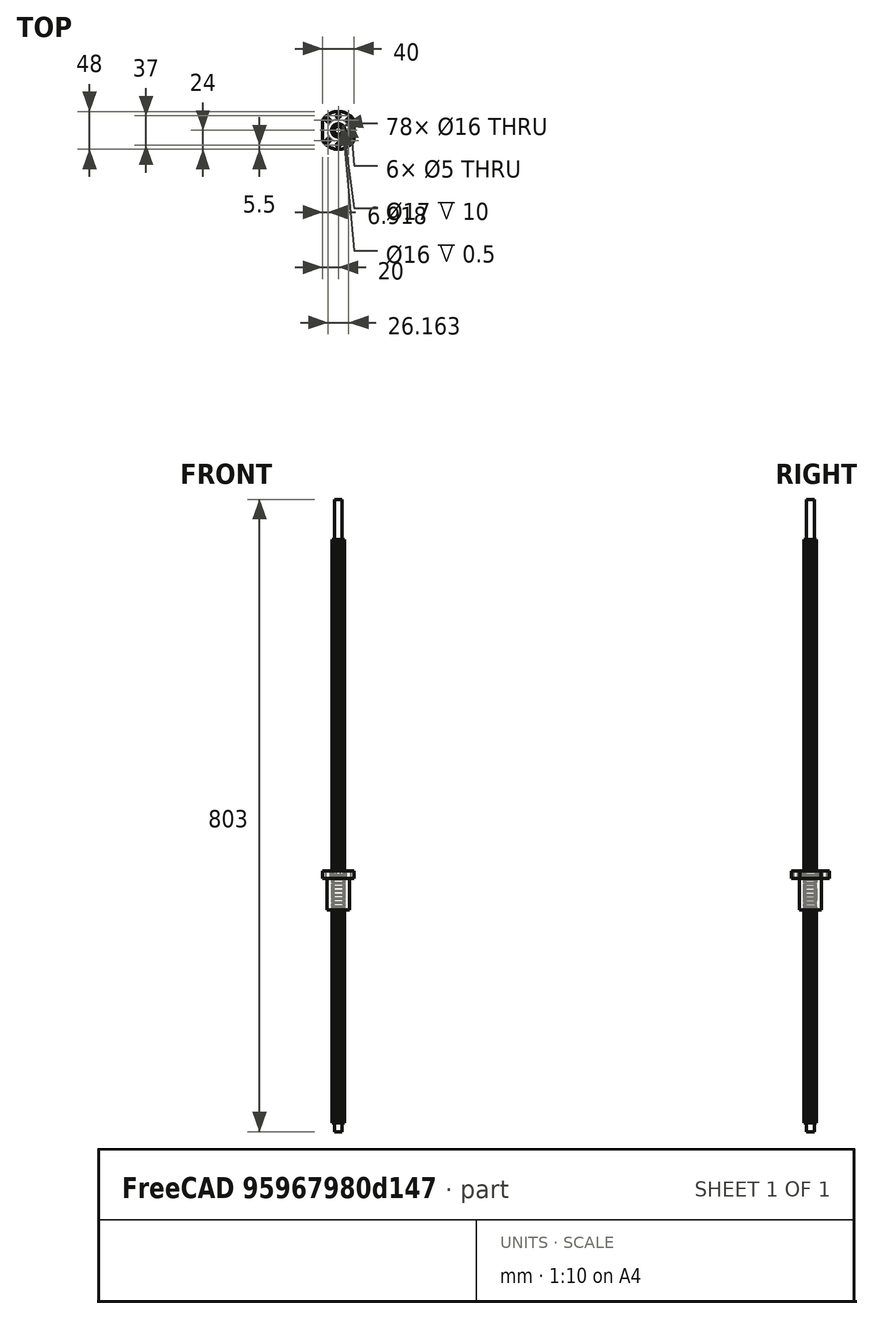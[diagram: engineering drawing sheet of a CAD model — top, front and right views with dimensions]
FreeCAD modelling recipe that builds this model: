
FCSTD DOCUMENT  (FreeCAD 0.14R3702 (Git))
Label: simple_ballscrew
License: CC-BY 3.0
LicenseURL: http://creativecommons.org/licenses/by/3.0/
objects: Sketcher::SketchObject×2, PartDesign::Pad×2, Part::Feature×1, Part::Torus×1, Part::FeaturePython×1, Part::Cut×1, Part::MultiFuse×1
note: 11 computed .brp shape members not serialized (recipe doc carries the construction recipe); baked Part::Feature solids carry a one-line shape summary decoded from their .brp

FEATURE [Sketcher::SketchObject] Sketch
  sketch-geometry (1):
    g0: Circle CenterX=0 CenterY=0 CenterZ=0 NormalX=0 NormalY=0 NormalZ=1 Radius=8
  constraints (2):
    c: Coincident(g0,g-1)
    c: Radius(g0) = 8
FEATURE [PartDesign::Pad] Pad001
  Length = 741
  Length2 = 1
  Sketch = -> Sketch
  Type = 0
FEATURE [Sketcher::SketchObject] Sketch001
  Placement = pos=(0,0,0) rot=(1,0,0;3.14159rad)
  Support = -> Pad001 [Face2]
  sketch-geometry (1):
    g0: Circle CenterX=0 CenterY=0 CenterZ=0 NormalX=0 NormalY=0 NormalZ=1 Radius=5
  constraints (2):
    c: Coincident(g0,g-1)
    c: Radius(g0) = 5
FEATURE [PartDesign::Pad] Pad002  label="Pad004"
  Length = 11
  Length2 = 792
  Sketch = -> Sketch001
  Type = 4
FEATURE [Part::Feature] Pad003  label="Pad002"
  Placement = pos=(0,0,320.5) rot=(1,0,0;3.14159rad)
  shape: bbox 40 x 48 x 50 mm, 17 faces (baked)
FEATURE [Part::Torus] Torus
  Angle1 = -180
  Angle2 = 180
  Angle3 = 360
  Placement = pos=(0,0,2) rot=(0,0,1;0rad)
  Radius1 = 8
  Radius2 = 2
FEATURE [Part::FeaturePython] Array  # Draft array (typed FeaturePython)
  Angle = 360
  ArrayType = 0
  Axis = (0,0,1)
  Base = -> Torus
  Center = (0,0,0)
  IntervalX = (1,0,0)
  IntervalY = (0,1,0)
  IntervalZ = (0,0,5)
  NumberPolar = 1
  NumberX = 1
  NumberY = 1
  NumberZ = 148
FEATURE [Part::Cut] Cut
  Base = -> Pad002
  Tool = -> Array
FEATURE [Part::MultiFuse] Fusion
  Shapes = -> [Pad003,Cut]
